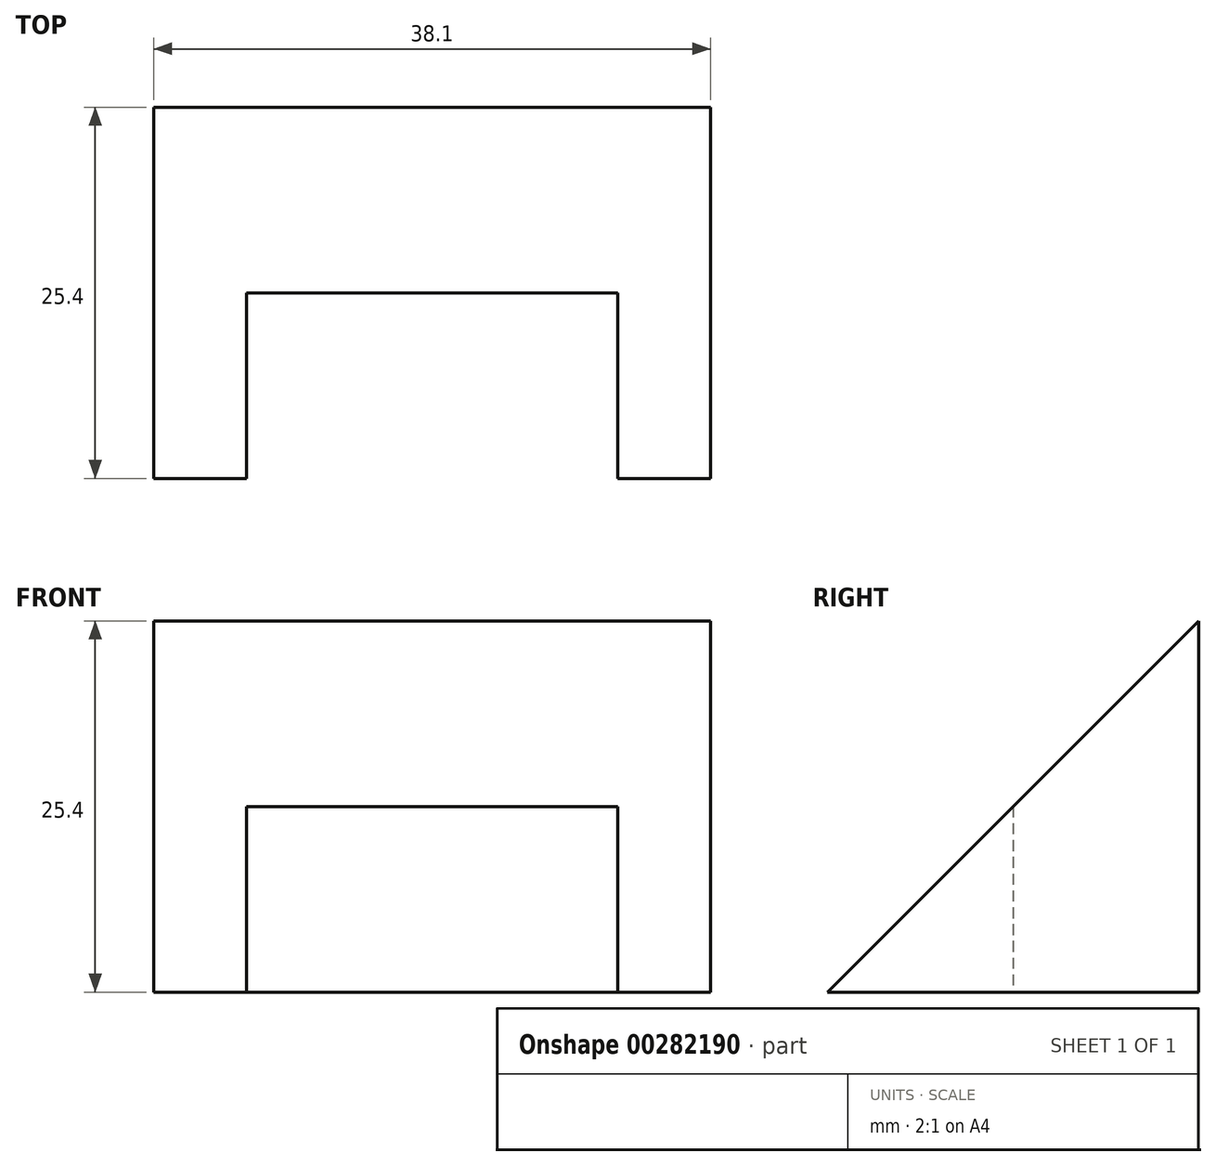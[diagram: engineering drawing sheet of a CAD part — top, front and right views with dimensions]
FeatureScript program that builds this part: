
annotation { "Feature Type Name" : "Feature", "Feature Type Description" : "" }
export const myFeature = defineFeature(function(context is Context, id is Id, definition is map)
    precondition{}
    {
        {
            var Q0;
            Q0=qCreatedBy(makeId("Right.planeOp"),FACE);
            var sketch = newSketch(context, id + "F0", { "sketchPlane" : qUnion([Q0])});
            skLineSegment(sketch, "E0", {"start": v(0, 0) * mm, "end": v(0, 25.4) * mm});
            skLineSegment(sketch, "E1", {"start": v(0, 25.4) * mm, "end": v(-25.4, 0) * mm});
            skLineSegment(sketch, "E2", {"start": v(-25.4, 0) * mm, "end": v(0, 0) * mm});
            skSolve(sketch);
        }
        {
            var Q0;
            Q0=makeQuery(id+"F0.imprint","IMPRINT",FACE,{"disambiguationData":[TD([[makeQuery(id+"F0.imprint","IMPRINT",EDGE,{"derivedFrom":sQuery(id+"F0.wireOp",EDGE,"E0")}),1.0]])]});
            extrude(context, id + "F1", {"entities" : qUnion([Q0]), "depth" : 38.1 * mm});
        }
        {
            var Q0;
            Q0=makeQuery(id+"F1.opExtrude","SWEPT_FACE",FACE,{"disambiguationData":[OSD([sQuery(id+"F0.wireOp",EDGE,"E2")])]});
            var sketch = newSketch(context, id + "F2", { "sketchPlane" : qUnion([Q0])});
            skLineSegment(sketch, "E3.bottom", {"start": v(6.35, 25.4) * mm, "end": v(31.75, 25.4) * mm});
            skLineSegment(sketch, "E3.top", {"start": v(6.35, 12.7) * mm, "end": v(31.75, 12.7) * mm});
            skLineSegment(sketch, "E3.left", {"start": v(6.35, 25.4) * mm, "end": v(6.35, 12.7) * mm});
            skLineSegment(sketch, "E3.right", {"start": v(31.75, 25.4) * mm, "end": v(31.75, 12.7) * mm});
            skSolve(sketch);
        }
        {
            var Q0;
            Q0=makeQuery(id+"F2.imprint","IMPRINT",FACE,{"disambiguationData":[TD([[makeQuery(id+"F2.imprint","IMPRINT",EDGE,{"derivedFrom":sQuery(id+"F2.wireOp",EDGE,"E3.bottom")}),1.0]])]});
            extrude(context, id + "F3", {"entities" : qUnion([Q0]), "operationType" : NewBodyOperationType.REMOVE, "oppositeDirection" : true, "depth" : 25.4 * mm});
        }
    });
